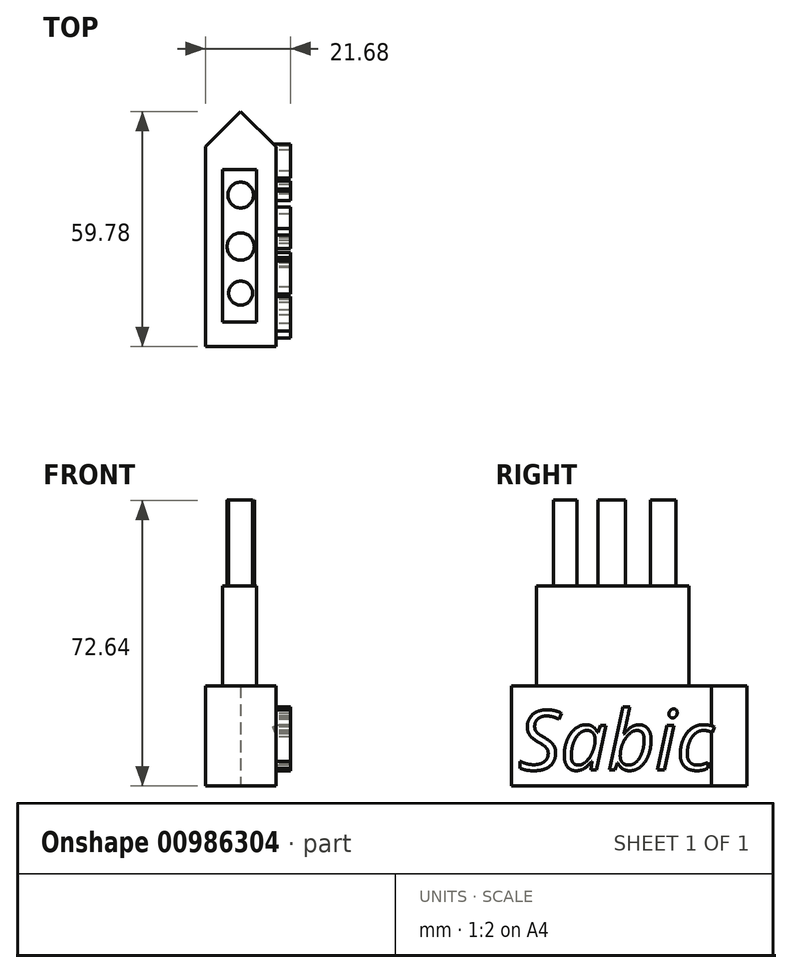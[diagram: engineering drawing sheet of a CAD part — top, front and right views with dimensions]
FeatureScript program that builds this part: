
annotation { "Feature Type Name" : "Feature", "Feature Type Description" : "" }
export const myFeature = defineFeature(function(context is Context, id is Id, definition is map)
    precondition{}
    {
        {
            var Q0;
            Q0=qCreatedBy(makeId("Top.planeOp"),FACE);
            var sketch = newSketch(context, id + "F0", { "sketchPlane" : qUnion([Q0])});
            skLineSegment(sketch, "E0", {"start": v(-8.98, -28.24) * mm, "end": v(-8.98, 22.56) * mm});
            skLineSegment(sketch, "E1", {"start": v(-8.98, 22.56) * mm, "end": v(0, 31.54) * mm});
            skLineSegment(sketch, "E2", {"start": v(0, 31.54) * mm, "end": v(8.98, 22.56) * mm});
            skLineSegment(sketch, "E3", {"start": v(8.98, 22.56) * mm, "end": v(8.98, -28.24) * mm});
            skLineSegment(sketch, "E4", {"start": v(8.98, -28.24) * mm, "end": v(-8.98, -28.24) * mm});
            skSolve(sketch);
        }
        {
            var Q0;
            Q0 = qSketchRegion(id + "F0", true);
            extrude(context, id + "F1", {"entities" : qUnion([Q0]), "depth" : 25.4 * mm, "offsetDistance" : 25.4 * mm});
        }
        {
            var Q0;
            Q0=makeQuery(id+"F1.opExtrude","CAP_FACE",FACE,{"disambiguationData":[OSD([sQuery(id+"F0.wireOp",EDGE,"E0"),sQuery(id+"F0.wireOp",EDGE,"E1"),sQuery(id+"F0.wireOp",EDGE,"E2"),sQuery(id+"F0.wireOp",EDGE,"E3"),sQuery(id+"F0.wireOp",EDGE,"E4")])],"isStart":false});
            var sketch = newSketch(context, id + "F2", { "sketchPlane" : qUnion([Q0])});
            skLineSegment(sketch, "E5.bottom", {"start": v(-4.6, 16.77) * mm, "end": v(4, 16.77) * mm});
            skLineSegment(sketch, "E5.top", {"start": v(-4.6, -21.95) * mm, "end": v(4, -21.95) * mm});
            skLineSegment(sketch, "E5.left", {"start": v(-4.6, 16.77) * mm, "end": v(-4.6, -21.95) * mm});
            skLineSegment(sketch, "E5.right", {"start": v(4, 16.77) * mm, "end": v(4, -21.95) * mm});
            skSolve(sketch);
        }
        {
            var Q0;
            Q0 = qSketchRegion(id + "F2", true);
            extrude(context, id + "F3", {"entities" : qUnion([Q0]), "operationType" : NewBodyOperationType.ADD, "depth" : 25.4 * mm, "offsetDistance" : 25.4 * mm});
        }
        {
            var Q0;
            Q0=qCreatedBy(makeId("Top.planeOp"),FACE);
            var sketch = newSketch(context, id + "F4", { "sketchPlane" : qUnion([Q0])});
            skCircle(sketch, "E6", {"center": v(0, 10.29) * mm, "radius": 3.26 * mm});
            skCircle(sketch, "E7", {"center": v(0, -14.6) * mm, "radius": 3.04 * mm});
            skCircle(sketch, "E8", {"center": v(0, -2.8) * mm, "radius": 3.47 * mm});
            skSolve(sketch);
        }
        {
            var Q0;
            Q0 = qSketchRegion(id + "F4", true);
            extrude(context, id + "F5", {"entities" : qUnion([Q0]), "operationType" : NewBodyOperationType.ADD, "depth" : 72.64 * mm, "offsetDistance" : 25.4 * mm});
        }
        {
            var Q0;
            Q0=qCreatedBy(makeId("Right.planeOp"),FACE);
            var sketch = newSketch(context, id + "F6", { "sketchPlane" : qUnion([Q0])});
            skText(sketch, "E9", { "text": "Sabic", "fontName": "OpenSans-Italic.ttf"});
            const initialGuessF6  = {"E9": [-0.02646, 0.00411, 1, 0, 0.0152]};
            skSetInitialGuess(sketch, initialGuessF6);
            skSolve(sketch);
        }
        {
            var Q0;
            Q0 = qSketchRegion(id + "F6", true);
            extrude(context, id + "F7", {"entities" : qUnion([Q0]), "operationType" : NewBodyOperationType.ADD, "depth" : 12.7 * mm, "offsetDistance" : 25.4 * mm});
        }
    });
